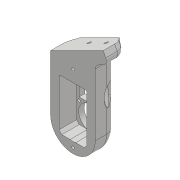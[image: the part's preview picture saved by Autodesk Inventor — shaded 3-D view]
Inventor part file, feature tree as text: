
AUTODESK INVENTOR PART (.ipt)
format: ipt  version: 2018 (Build 220112000, 112)  size: 902,144 bytes
history: native  units: mm
features: sketch x31, projected_geometry x26, extrude x24, hole x10, fillet x10, chamfer x3, mirror x1, plane x1
ambient origin geometry x8: Origin, YZ Plane, XZ Plane, XY Plane, X Axis, Y Axis, Z Axis, Center Point
bodies: Solid1 (feature_tree)
feature tree (106):
  extrude  "Extrusion1"  Depth=45.0mm
  extrude  "Extrusion2"  Depth=2.25mm
  hole  "Hole1"  [1 undecoded]
  hole  "Hole2"  [1 undecoded]
  fillet  "Fillet1"  Radius=14.0mm
  extrude  "Extrusion3"  Depth=18.5mm
  extrude  "Extrusion4"  Depth=10.0mm
  extrude  "Extrusion5"  Depth=2.195mm
  extrude  "Extrusion6"  Depth=20.5mm
  hole  "Hole3"  [1 undecoded]
  extrude  "Extrusion7"  Depth=0.5mm
  extrude  "Extrusion8"  Depth=5.0mm TaperAngle=0.0deg
  extrude  "Extrusion9"  Depth=10.0mm
  extrude  "Extrusion10"  Depth=10.0mm
  extrude  "Extrusion11"  Depth=14.5mm
  extrude  "Extrusion12"  Depth=20.0mm
  extrude  "Extrusion13"  Depth=5.0mm
  extrude  "Extrusion14"  Depth=5.0mm
  extrude  "Extrusion15"  Depth=5.0mm
  extrude  "Extrusion16"  Depth=5.0mm
  extrude  "Extrusion17"  Depth=4.0mm
  chamfer  "Chamfer1"  Distance=1.0mm
  fillet  "Fillet7"  Radius=20.7mm
  fillet  "Fillet8"  Radius=32.0mm
  mirror  "Mirror1"
  extrude  "Extrusion24"  Depth=5.0mm TaperAngle=0.0deg
  extrude  "Extrusion25"  Depth=8.0mm
  extrude  "Extrusion26"  Depth=0.2mm TaperAngle=0.0deg
  extrude  "Extrusion27"  Depth=0.5mm TaperAngle=0.0deg
  extrude  "Extrusion28"  Depth=5.0mm TaperAngle=0.0deg
  chamfer  "Chamfer5"  Distance=5.0mm
  fillet  "Fillet18"  Radius=0.2mm
  fillet  "Fillet19"  Radius=0.2mm
  extrude  "Extrusion29"  Depth=1.5mm
  chamfer  "Chamfer6"  Distance=70.0mm
  hole  "Hole10"  [1 undecoded]
  plane  "Work Plane2"
  hole  "Hole11"  [1 undecoded]
  fillet  "Fillet20"  Radius=10.0mm
  sketch  "Sketch43"  dims[d102=2.5mm d103=2.0mm d104=45.0deg d105=1.5mm]
  hole  "Hole12"  [1 undecoded]
  hole  "Hole13"  [1 undecoded]
  hole  "Hole14"  [1 undecoded]
  fillet  "Fillet21"  Radius=10.0mm
  fillet  "Fillet22"  Radius=2.0mm
  hole  "Hole15"  [1 undecoded]
  fillet  "Fillet23"  Radius=5.0mm
  hole  "Hole16"  [1 undecoded]
  fillet  "Fillet24"  Radius=15.0mm
  extrude  "Extrusion30"  Depth=10.0mm TaperAngle=0.0deg
  sketch  "Sketch1"  dims[d0=24.5mm d1=45.0mm]
  sketch  "Sketch2"  dims[d2=1.95mm d3=0.0mm d4=2.25mm]
  projected_geometry  "Projected Loop1"
  sketch  "Sketch3"  dims[d5=20.0mm d6=2.25mm]
  projected_geometry  "Projected Loop2"
  sketch  "Sketch4"  dims[d7=5.25mm d8=5.25mm d9=14.0mm]
  projected_geometry  "Projected Loop3"
  sketch  "Sketch5"  dims[d10=5.25mm d11=18.5mm]
  projected_geometry  "Projected Loop4"
  sketch  "Sketch6"  dims[d12=10.0mm d13=0.0mm d14=20.5mm]
  projected_geometry  "Projected Loop5"
  sketch  "Sketch7"  dims[d15=2.0mm d16=2.195mm]
  projected_geometry  "Projected Loop6"
  sketch  "Sketch8"  dims[d17=2.0mm]
  projected_geometry  "Projected Loop7"
  sketch  "Sketch9"  dims[d18=2.4mm d19=6.0mm d20=4.4mm d21=2.0mm d22=90.0deg d23=8.0mm d24=20.594885mm d25=20.5mm]
  projected_geometry  "Projected Loop8"
  projected_geometry  "Projected Loop9"
  sketch  "Sketch10"  dims[d26=26.65mm d27=2.0mm]
  projected_geometry  "Projected Loop10"
  projected_geometry  "Projected Loop11"
  sketch  "Sketch11"  dims[d28=2.0mm]
  projected_geometry  "Projected Loop12"
  sketch  "Sketch12"  dims[d29=2.4mm d30=6.0mm d31=4.4mm d32=2.0mm d33=90.0deg d34=8.0mm d35=20.594885mm d36=0.5mm]
  sketch  "Sketch13"  dims[d37=18.0mm d38=5.0mm d39=0.0mm]
  sketch  "Sketch14"  dims[d41=10.0mm d42=0.0mm d43=24.5mm]
  projected_geometry  "Projected Loop13"
  sketch  "Sketch15"  dims[d44=1.15mm d45=0.0mm d46=10.0mm]
  sketch  "Sketch16"  dims[d47=21.0mm d48=14.5mm]
  projected_geometry  "Projected Loop14"
  sketch  "Sketch17"  dims[d49=20.0mm d50=14.5mm]
  projected_geometry  "Projected Loop15"
  sketch  "Sketch18"  dims[d51=24.5mm d52=5.0mm]
  projected_geometry  "Projected Loop16"
  sketch  "Sketch19"  dims[d53=5.0mm d54=2.25mm]
  projected_geometry  "Projected Loop17"
  sketch  "Sketch20"  dims[d55=2.25mm d56=5.0mm]
  projected_geometry  "Projected Loop18"
  sketch  "Sketch35"  dims[d57=5.0mm d58=9.0mm]
  projected_geometry  "Projected Loop28"
  sketch  "Sketch36"  dims[d59=14.75mm d60=4.0mm d61=1.0mm d62=0.0mm d63=20.7mm]
  projected_geometry  "Projected Loop29"
  sketch  "Sketch37"  dims[d64=2.4mm d65=6.0mm d66=4.4mm d67=2.0mm d68=90.0deg d69=8.0mm d70=20.594885mm d72=32.0mm]
  sketch  "Sketch38"  dims[d73=5.0mm d74=0.0mm d75=1.0mm d76=0.0mm]
  sketch  "Sketch39"  dims[d77=12.25mm d78=0.0mm d80=8.0mm]
  projected_geometry  "Projected Loop30"
  sketch  "Sketch40"  dims[d81=4.5mm d82=0.0mm d84=0.2mm d85=0.0mm]
  projected_geometry  "Projected Loop31"
  sketch  "Sketch41"  dims[d86=21.0mm d87=0.5mm d88=0.0mm]
  projected_geometry  "Projected Loop32"
  projected_geometry  "Projected Loop33"
  sketch  "Sketch42"  dims[d91=8.0mm d92=0.0mm d93=5.0mm d94=0.0mm d95=5.0mm d96=0.0mm d98=0.2mm d99=0.0mm d100=0.2mm d101=0.0mm]
  projected_geometry  "Projected Loop34"
  sketch  "Sketch44"  dims[d114=0.5mm]
  projected_geometry  "Projected Loop35"
  sketch  "Sketch45"  dims[d187=40.0mm d188=70.0mm d189=20.0mm d190=10.0mm d191=0.0mm d192=10.0mm d193=0.0mm d194=2.0mm d195=0.0mm d196=2.0mm d197=0.0mm d198=8.0mm d199=10.0mm d200=2.0mm d201=0.0mm d204=7.0mm d205=2.0mm d206=45.0deg d207=5.0mm d208=8.0mm d209=15.0mm d210=2.0mm d211=0.0mm d212=1.5mm d213=2.0mm d214=45.0deg d215=24.0mm d216=17.0mm d217=3.5mm d218=3.2mm d219=6.0mm d220=9.4mm d221=2.0mm d222=90.0deg d223=8.0mm d224=20.594885mm d225=6.0mm d226=6.0mm d227=9.4mm d228=2.0mm d229=90.0deg d230=69.0mm d231=0.0mm d232=1.0mm d233=8.0mm d234=2.459mm d235=6.0mm d236=9.4mm d237=2.0mm d238=90.0deg d239=34.0mm d240=20.594885mm d241=3.2mm d242=6.0mm d243=6.3mm d244=2.0mm d245=90.0deg d246=20.55mm d247=0.0mm d248=6.0mm d249=6.0mm d250=6.3mm d251=2.0mm d252=90.0deg d253=10.0mm d254=0.0mm d255=1.5mm d256=0.75mm d257=4.0mm d258=6.0mm d259=4.4mm d260=2.0mm d261=90.0deg d262=2.5mm d263=0.0mm d264=1.0mm d265=4.0mm d266=6.0mm d267=4.4mm d268=2.0mm d269=90.0deg d270=2.5mm d271=0.0mm d272=1.0mm d273=20.55mm d274=0.0mm]
note: 10 required parameter values undecoded (feature->parameter linkage not recoverable at this tier; creation-order binding heuristic only, values carry confidence <= 0.55)
